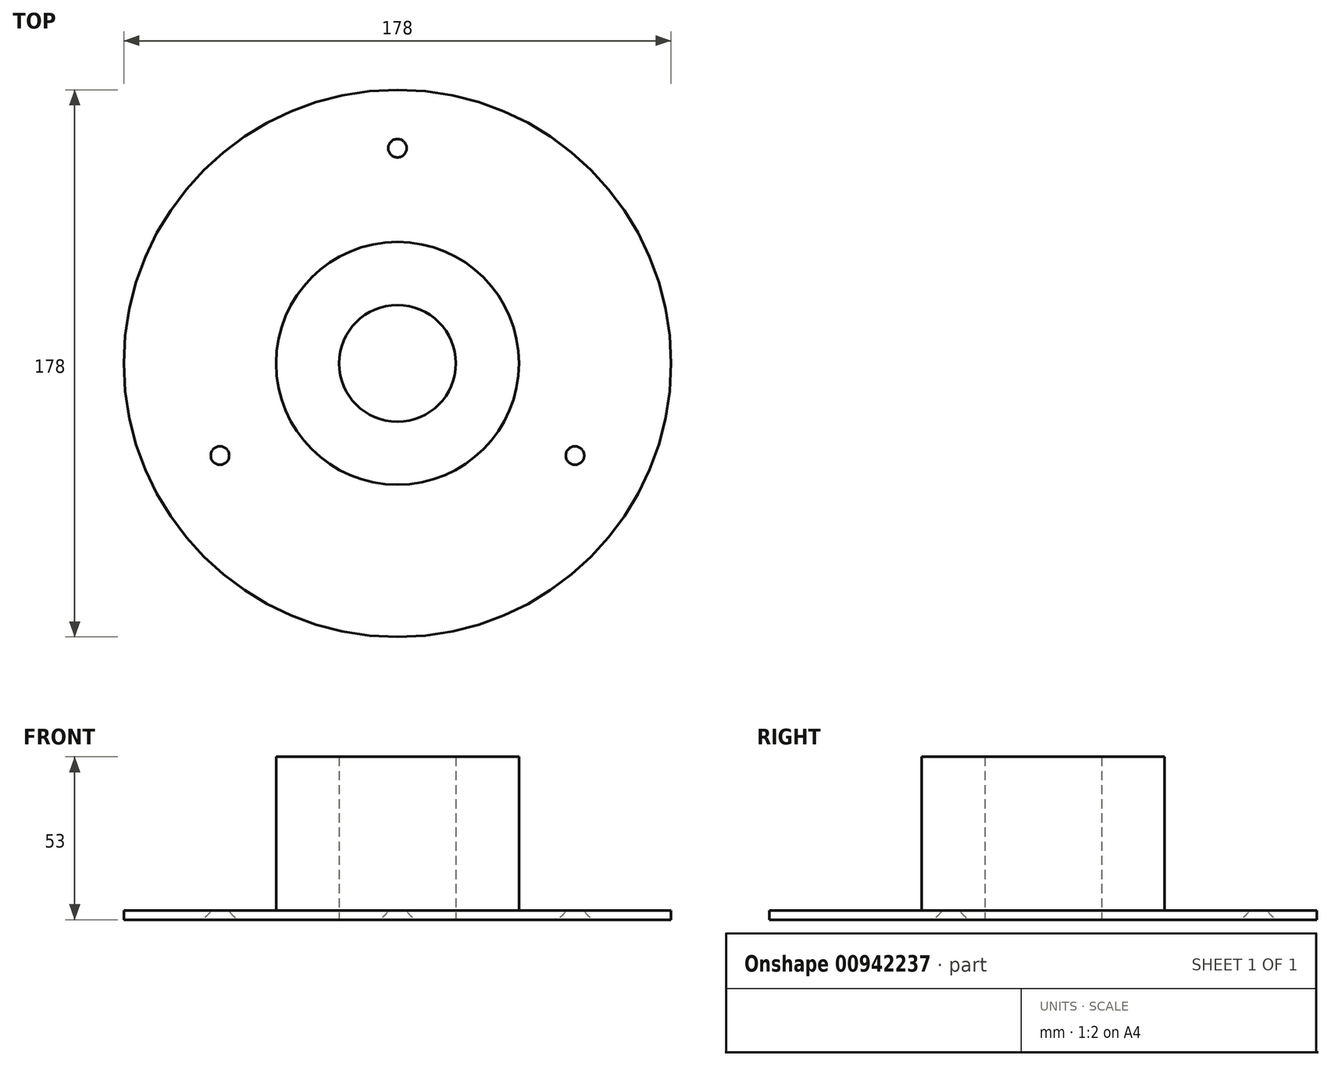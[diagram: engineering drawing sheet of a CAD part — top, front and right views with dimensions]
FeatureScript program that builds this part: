
annotation { "Feature Type Name" : "Feature", "Feature Type Description" : "" }
export const myFeature = defineFeature(function(context is Context, id is Id, definition is map)
    precondition{}
    {
        {
            var Q0;
            Q0=qCreatedBy(makeId("Top.planeOp"),FACE);
            var sketch = newSketch(context, id + "F0", { "sketchPlane" : qUnion([Q0])});
            skCircle(sketch, "E0", {"center": v(0, 0) * mm, "radius": 89 * mm});
            skCircle(sketch, "E1", {"center": v(0, 0) * mm, "radius": 19 * mm});
            skLineSegment(sketch, "E2", {"start": v(0, -74.62) * mm, "end": v(0, 86.92) * mm, "construction": true});
            skLineSegment(sketch, "E3", {"start": v(83.16, 0) * mm, "end": v(-80.72, 0) * mm, "construction": true});
            skCircle(sketch, "E4", {"center": v(0, 70) * mm, "radius": 3 * mm});
            skCircle(sketch, "E5.1.0", {"center": v(-57.74, -30) * mm, "radius": 3 * mm});
            skCircle(sketch, "E5.2.0", {"center": v(57.74, -30) * mm, "radius": 3 * mm});
            skPoint(sketch, "E5.center", {"position": v(0, 3.33) * mm});
            skSolve(sketch);
        }
        {
            var Q0;
            Q0 = qSketchRegion(id + "F0", true);
            extrude(context, id + "F1", {"entities" : qUnion([Q0]), "depth" : 3 * mm, "offsetDistance" : 25 * mm});
        }
        {
            var Q0;
            Q0=makeQuery(id+"F1.opExtrude","CAP_FACE",FACE,{"disambiguationData":[OSD([sQuery(id+"F0.wireOp",EDGE,"E0"),sQuery(id+"F0.wireOp",EDGE,"E1"),sQuery(id+"F0.wireOp",EDGE,"E4"),sQuery(id+"F0.wireOp",EDGE,"E5.1.0"),sQuery(id+"F0.wireOp",EDGE,"E5.2.0")])],"isStart":false});
            var sketch = newSketch(context, id + "F2", { "sketchPlane" : qUnion([Q0])});
            skCircle(sketch, "E6", {"center": v(0, 0) * mm, "radius": 19 * mm});
            skCircle(sketch, "E7", {"center": v(0, 0) * mm, "radius": 39.5 * mm});
            skSolve(sketch);
        }
        {
            var Q0;
            Q0 = qSketchRegion(id + "F2", true);
            extrude(context, id + "F3", {"entities" : qUnion([Q0]), "operationType" : NewBodyOperationType.ADD, "depth" : 50 * mm, "offsetDistance" : 25 * mm});
        }
        {
            var Q0;
            Q0=makeQuery(id+"F1.opExtrude","CAP_EDGE",EDGE,{"disambiguationData":[OSD([sQuery(id+"F0.wireOp",EDGE,"E5.2.0")])],"isStart":true});
            var Q1;
            Q1=makeQuery(id+"F1.opExtrude","CAP_EDGE",EDGE,{"disambiguationData":[OSD([sQuery(id+"F0.wireOp",EDGE,"E4")])],"isStart":true});
            var Q2;
            Q2=makeQuery(id+"F1.opExtrude","CAP_EDGE",EDGE,{"disambiguationData":[OSD([sQuery(id+"F0.wireOp",EDGE,"E5.1.0")])],"isStart":true});
            fillet(context, id + "F4", {"entities" : qUnion([Q0, Q1, Q2]), "radius" : 5 * mm, "tangentPropagation" : true, "allowEdgeOverflow" : false});
        }
    });
